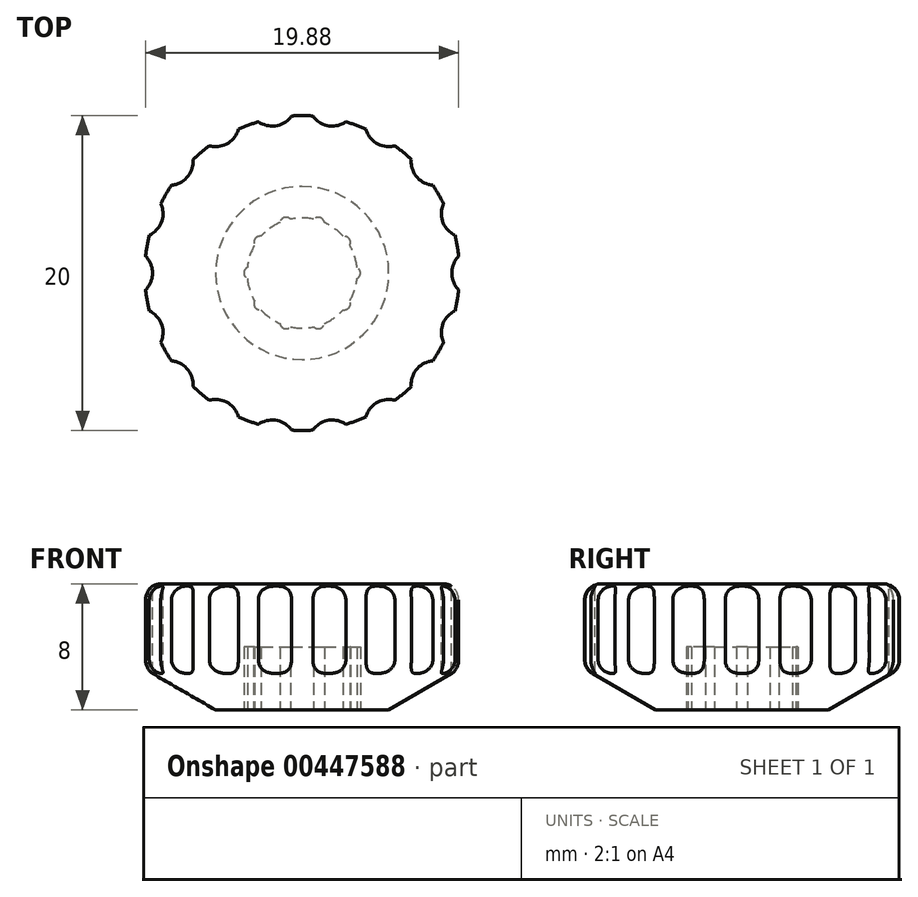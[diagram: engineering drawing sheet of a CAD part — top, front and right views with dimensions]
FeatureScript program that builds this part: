
annotation { "Feature Type Name" : "Feature", "Feature Type Description" : "" }
export const myFeature = defineFeature(function(context is Context, id is Id, definition is map)
    precondition{}
    {
        {
            var Q0;
            Q0=qCreatedBy(makeId("Right.planeOp"),FACE);
            var sketch = newSketch(context, id + "F0", { "sketchPlane" : qUnion([Q0])});
            skLineSegment(sketch, "E0", {"start": v(0, -2.01) * mm, "end": v(0, 9.16) * mm, "construction": true});
            skLineSegment(sketch, "E1.bottom", {"start": v(0, 8) * mm, "end": v(-10, 8) * mm});
            skLineSegment(sketch, "E1.top", {"start": v(-3.5, 0) * mm, "end": v(-5.5, 0) * mm});
            skLineSegment(sketch, "E1.left", {"start": v(0, 8) * mm, "end": v(0, 4) * mm});
            skLineSegment(sketch, "E1.right", {"start": v(-10, 8) * mm, "end": v(-10, 2.6) * mm});
            skLineSegment(sketch, "E2.top", {"start": v(0, 4) * mm, "end": v(-3.5, 4) * mm});
            skLineSegment(sketch, "E2.right", {"start": v(-3.5, 0) * mm, "end": v(-3.5, 4) * mm});
            skLineSegment(sketch, "E3", {"start": v(-10, 2.6) * mm, "end": v(-5.5, 0) * mm});
            skSolve(sketch);
        }
        {
            var Q0;
            Q0 = qSketchRegion(id + "F0", true);
            var Q1;
            Q1=sQuery(id+"F0.wireOp",EDGE,"E0");
            revolve(context, id + "F1", {"entities" : qUnion([Q0]), "axis" : qUnion([Q1]), "revolveType" : RevolveType.FULL});
        }
        {
            var Q0;
            Q0=makeQuery(id+"F1.opRevolve","SWEPT_EDGE",EDGE,{"disambiguationData":[OSD([sQuery(id+"F0.wireOp",EDGE,"E1.bottom"),sQuery(id+"F0.wireOp",EDGE,"E1.right")])]});
            var Q1;
            Q1=makeQuery(id+"F1.opRevolve","SWEPT_EDGE",EDGE,{"disambiguationData":[OSD([sQuery(id+"F0.wireOp",EDGE,"E1.right"),sQuery(id+"F0.wireOp",EDGE,"E3")])]});
            fillet(context, id + "F2", {"entities" : qUnion([Q0, Q1]), "radius" : 1 * mm, "tangentPropagation" : true, "allowEdgeOverflow" : false});
        }
        {
            var Q0;
            Q0=makeQuery(id+"F1.opRevolve","SWEPT_FACE",FACE,{"disambiguationData":[OSD([sQuery(id+"F0.wireOp",EDGE,"E1.top")])]});
            var sketch = newSketch(context, id + "F3", { "sketchPlane" : qUnion([Q0])});
            skCircle(sketch, "E4", {"center": v(-3.3, 0) * mm, "radius": 0.4 * mm});
            skCircle(sketch, "E5.1.0", {"center": v(-2.67, -1.94) * mm, "radius": 0.4 * mm});
            skCircle(sketch, "E5.2.0", {"center": v(-1.02, -3.14) * mm, "radius": 0.4 * mm});
            skCircle(sketch, "E5.3.0", {"center": v(1.02, -3.14) * mm, "radius": 0.4 * mm});
            skCircle(sketch, "E5.4.0", {"center": v(2.67, -1.94) * mm, "radius": 0.4 * mm});
            skCircle(sketch, "E5.5.0", {"center": v(3.3, 0) * mm, "radius": 0.4 * mm});
            skCircle(sketch, "E5.6.0", {"center": v(2.67, 1.94) * mm, "radius": 0.4 * mm});
            skCircle(sketch, "E5.7.0", {"center": v(1.02, 3.14) * mm, "radius": 0.4 * mm});
            skCircle(sketch, "E5.8.0", {"center": v(-1.02, 3.14) * mm, "radius": 0.4 * mm});
            skCircle(sketch, "E5.9.0", {"center": v(-2.67, 1.94) * mm, "radius": 0.4 * mm});
            skPoint(sketch, "E5.center", {"position": v(0, 0) * mm});
            skSolve(sketch);
        }
        {
            var Q0;
            {var subQ0=sQuery(id+"F3.wireOp",EDGE,"E4");var subQ1=makeQuery(id+"F1.opRevolve","SWEPT_EDGE",EDGE,{"disambiguationData":[OSD([sQuery(id+"F0.wireOp",EDGE,"E1.top"),sQuery(id+"F0.wireOp",EDGE,"E2.right")])]});var subQ2=makeQuery(id+"F3.imprint","INTERSECT",VERTEX,{"disambiguationData":[OD(0.0)],"derivedFrom":[subQ1,subQ0]});Q0=makeQuery(id+"F3.imprint","IMPRINT",FACE,{"disambiguationData":[TD([[makeQuery(id+"F3.imprint","IMPRINT",EDGE,{"disambiguationData":[TD([[subQ2,-1.0]])],"derivedFrom":subQ0}),1.0]])]});}
            var Q1;
            {var subQ0=sQuery(id+"F3.wireOp",EDGE,"E5.9.0");var subQ1=makeQuery(id+"F1.opRevolve","SWEPT_EDGE",EDGE,{"disambiguationData":[OSD([sQuery(id+"F0.wireOp",EDGE,"E1.top"),sQuery(id+"F0.wireOp",EDGE,"E2.right")])]});var subQ2=makeQuery(id+"F3.imprint","INTERSECT",VERTEX,{"disambiguationData":[OD(0.0)],"derivedFrom":[subQ1,subQ0]});Q1=makeQuery(id+"F3.imprint","IMPRINT",FACE,{"disambiguationData":[TD([[makeQuery(id+"F3.imprint","IMPRINT",EDGE,{"disambiguationData":[TD([[subQ2,1.0]])],"derivedFrom":subQ0}),1.0]])]});}
            var Q2;
            {var subQ0=sQuery(id+"F3.wireOp",EDGE,"E5.8.0");var subQ1=makeQuery(id+"F1.opRevolve","SWEPT_EDGE",EDGE,{"disambiguationData":[OSD([sQuery(id+"F0.wireOp",EDGE,"E1.top"),sQuery(id+"F0.wireOp",EDGE,"E2.right")])]});var subQ2=makeQuery(id+"F3.imprint","INTERSECT",VERTEX,{"disambiguationData":[OD(0.0)],"derivedFrom":[subQ1,subQ0]});Q2=makeQuery(id+"F3.imprint","IMPRINT",FACE,{"disambiguationData":[TD([[makeQuery(id+"F3.imprint","IMPRINT",EDGE,{"disambiguationData":[TD([[subQ2,1.0]])],"derivedFrom":subQ0}),1.0]])]});}
            var Q3;
            {var subQ0=sQuery(id+"F3.wireOp",EDGE,"E5.7.0");var subQ1=makeQuery(id+"F1.opRevolve","SWEPT_EDGE",EDGE,{"disambiguationData":[OSD([sQuery(id+"F0.wireOp",EDGE,"E1.top"),sQuery(id+"F0.wireOp",EDGE,"E2.right")])]});var subQ2=makeQuery(id+"F3.imprint","INTERSECT",VERTEX,{"disambiguationData":[OD(0.0)],"derivedFrom":[subQ1,subQ0]});Q3=makeQuery(id+"F3.imprint","IMPRINT",FACE,{"disambiguationData":[TD([[makeQuery(id+"F3.imprint","IMPRINT",EDGE,{"disambiguationData":[TD([[subQ2,1.0]])],"derivedFrom":subQ0}),1.0]])]});}
            var Q4;
            {var subQ0=sQuery(id+"F3.wireOp",EDGE,"E5.6.0");var subQ1=makeQuery(id+"F1.opRevolve","SWEPT_EDGE",EDGE,{"disambiguationData":[OSD([sQuery(id+"F0.wireOp",EDGE,"E1.top"),sQuery(id+"F0.wireOp",EDGE,"E2.right")])]});var subQ2=makeQuery(id+"F3.imprint","INTERSECT",VERTEX,{"disambiguationData":[OD(0.0)],"derivedFrom":[subQ1,subQ0]});Q4=makeQuery(id+"F3.imprint","IMPRINT",FACE,{"disambiguationData":[TD([[makeQuery(id+"F3.imprint","IMPRINT",EDGE,{"disambiguationData":[TD([[subQ2,1.0]])],"derivedFrom":subQ0}),1.0]])]});}
            var Q5;
            {var subQ0=sQuery(id+"F3.wireOp",EDGE,"E5.5.0");var subQ1=makeQuery(id+"F1.opRevolve","SWEPT_EDGE",EDGE,{"disambiguationData":[OSD([sQuery(id+"F0.wireOp",EDGE,"E1.top"),sQuery(id+"F0.wireOp",EDGE,"E2.right")])]});var subQ2=makeQuery(id+"F3.imprint","INTERSECT",VERTEX,{"disambiguationData":[OD(0.0)],"derivedFrom":[subQ1,subQ0]});Q5=makeQuery(id+"F3.imprint","IMPRINT",FACE,{"disambiguationData":[TD([[makeQuery(id+"F3.imprint","IMPRINT",EDGE,{"disambiguationData":[TD([[subQ2,1.0]])],"derivedFrom":subQ0}),1.0]])]});}
            var Q6;
            {var subQ0=sQuery(id+"F3.wireOp",EDGE,"E5.4.0");var subQ1=makeQuery(id+"F1.opRevolve","SWEPT_EDGE",EDGE,{"disambiguationData":[OSD([sQuery(id+"F0.wireOp",EDGE,"E1.top"),sQuery(id+"F0.wireOp",EDGE,"E2.right")])]});var subQ2=makeQuery(id+"F3.imprint","INTERSECT",VERTEX,{"disambiguationData":[OD(0.0)],"derivedFrom":[subQ1,subQ0]});Q6=makeQuery(id+"F3.imprint","IMPRINT",FACE,{"disambiguationData":[TD([[makeQuery(id+"F3.imprint","IMPRINT",EDGE,{"disambiguationData":[TD([[subQ2,-1.0]])],"derivedFrom":subQ0}),1.0]])]});}
            var Q7;
            {var subQ0=sQuery(id+"F3.wireOp",EDGE,"E5.3.0");var subQ1=makeQuery(id+"F1.opRevolve","SWEPT_EDGE",EDGE,{"disambiguationData":[OSD([sQuery(id+"F0.wireOp",EDGE,"E1.top"),sQuery(id+"F0.wireOp",EDGE,"E2.right")])]});var subQ2=makeQuery(id+"F3.imprint","INTERSECT",VERTEX,{"disambiguationData":[OD(0.0)],"derivedFrom":[subQ1,subQ0]});Q7=makeQuery(id+"F3.imprint","IMPRINT",FACE,{"disambiguationData":[TD([[makeQuery(id+"F3.imprint","IMPRINT",EDGE,{"disambiguationData":[TD([[subQ2,-1.0]])],"derivedFrom":subQ0}),1.0]])]});}
            var Q8;
            {var subQ0=sQuery(id+"F3.wireOp",EDGE,"E5.2.0");var subQ1=makeQuery(id+"F1.opRevolve","SWEPT_EDGE",EDGE,{"disambiguationData":[OSD([sQuery(id+"F0.wireOp",EDGE,"E1.top"),sQuery(id+"F0.wireOp",EDGE,"E2.right")])]});var subQ2=makeQuery(id+"F3.imprint","INTERSECT",VERTEX,{"disambiguationData":[OD(0.0)],"derivedFrom":[subQ1,subQ0]});Q8=makeQuery(id+"F3.imprint","IMPRINT",FACE,{"disambiguationData":[TD([[makeQuery(id+"F3.imprint","IMPRINT",EDGE,{"disambiguationData":[TD([[subQ2,-1.0]])],"derivedFrom":subQ0}),1.0]])]});}
            var Q9;
            {var subQ0=sQuery(id+"F3.wireOp",EDGE,"E5.1.0");var subQ1=makeQuery(id+"F1.opRevolve","SWEPT_EDGE",EDGE,{"disambiguationData":[OSD([sQuery(id+"F0.wireOp",EDGE,"E1.top"),sQuery(id+"F0.wireOp",EDGE,"E2.right")])]});var subQ2=makeQuery(id+"F3.imprint","INTERSECT",VERTEX,{"disambiguationData":[OD(0.0)],"derivedFrom":[subQ1,subQ0]});Q9=makeQuery(id+"F3.imprint","IMPRINT",FACE,{"disambiguationData":[TD([[makeQuery(id+"F3.imprint","IMPRINT",EDGE,{"disambiguationData":[TD([[subQ2,-1.0]])],"derivedFrom":subQ0}),1.0]])]});}
            var Q10;
            Q10=makeQuery(id+"F1.opRevolve","SWEPT_FACE",FACE,{"disambiguationData":[OSD([sQuery(id+"F0.wireOp",EDGE,"E2.top")])]});
            extrude(context, id + "F4", {"entities" : qUnion([Q0, Q1, Q2, Q3, Q4, Q5, Q6, Q7, Q8, Q9]), "operationType" : NewBodyOperationType.REMOVE, "endBound" : BoundingType.UP_TO_SURFACE, "oppositeDirection" : true, "depth" : 25 * mm, "endBoundEntityFace" : qUnion([Q10]), "offsetDistance" : 25 * mm});
        }
        {
            var Q0;
            Q0=makeQuery(id+"F1.opRevolve","SWEPT_FACE",FACE,{"disambiguationData":[OSD([sQuery(id+"F0.wireOp",EDGE,"E1.bottom")])]});
            var sketch = newSketch(context, id + "F5", { "sketchPlane" : qUnion([Q0])});
            skCircle(sketch, "E6", {"center": v(11, 0) * mm, "radius": 1.5 * mm});
            skCircle(sketch, "E7.1.0", {"center": v(10.34, 3.76) * mm, "radius": 1.5 * mm});
            skCircle(sketch, "E7.2.0", {"center": v(8.43, 7.07) * mm, "radius": 1.5 * mm});
            skCircle(sketch, "E7.3.0", {"center": v(5.5, 9.53) * mm, "radius": 1.5 * mm});
            skCircle(sketch, "E7.4.0", {"center": v(1.91, 10.83) * mm, "radius": 1.5 * mm});
            skCircle(sketch, "E7.5.0", {"center": v(-1.91, 10.83) * mm, "radius": 1.5 * mm});
            skCircle(sketch, "E7.6.0", {"center": v(-5.5, 9.53) * mm, "radius": 1.5 * mm});
            skCircle(sketch, "E7.7.0", {"center": v(-8.43, 7.07) * mm, "radius": 1.5 * mm});
            skCircle(sketch, "E7.8.0", {"center": v(-10.34, 3.76) * mm, "radius": 1.5 * mm});
            skCircle(sketch, "E7.9.0", {"center": v(-11, 0) * mm, "radius": 1.5 * mm});
            skCircle(sketch, "E7.10.0", {"center": v(-10.34, -3.76) * mm, "radius": 1.5 * mm});
            skCircle(sketch, "E7.11.0", {"center": v(-8.43, -7.07) * mm, "radius": 1.5 * mm});
            skCircle(sketch, "E7.12.0", {"center": v(-5.5, -9.53) * mm, "radius": 1.5 * mm});
            skCircle(sketch, "E7.13.0", {"center": v(-1.91, -10.83) * mm, "radius": 1.5 * mm});
            skCircle(sketch, "E7.14.0", {"center": v(1.91, -10.83) * mm, "radius": 1.5 * mm});
            skCircle(sketch, "E7.15.0", {"center": v(5.5, -9.53) * mm, "radius": 1.5 * mm});
            skCircle(sketch, "E7.16.0", {"center": v(8.43, -7.07) * mm, "radius": 1.5 * mm});
            skCircle(sketch, "E7.17.0", {"center": v(10.34, -3.76) * mm, "radius": 1.5 * mm});
            skPoint(sketch, "E7.center", {"position": v(0, 0) * mm});
            skSolve(sketch);
        }
        {
            var Q0;
            Q0 = qSketchRegion(id + "F5", true);
            extrude(context, id + "F6", {"entities" : qUnion([Q0]), "operationType" : NewBodyOperationType.REMOVE, "endBound" : BoundingType.THROUGH_ALL, "oppositeDirection" : true, "depth" : 25 * mm, "offsetDistance" : 25 * mm});
        }
    });
